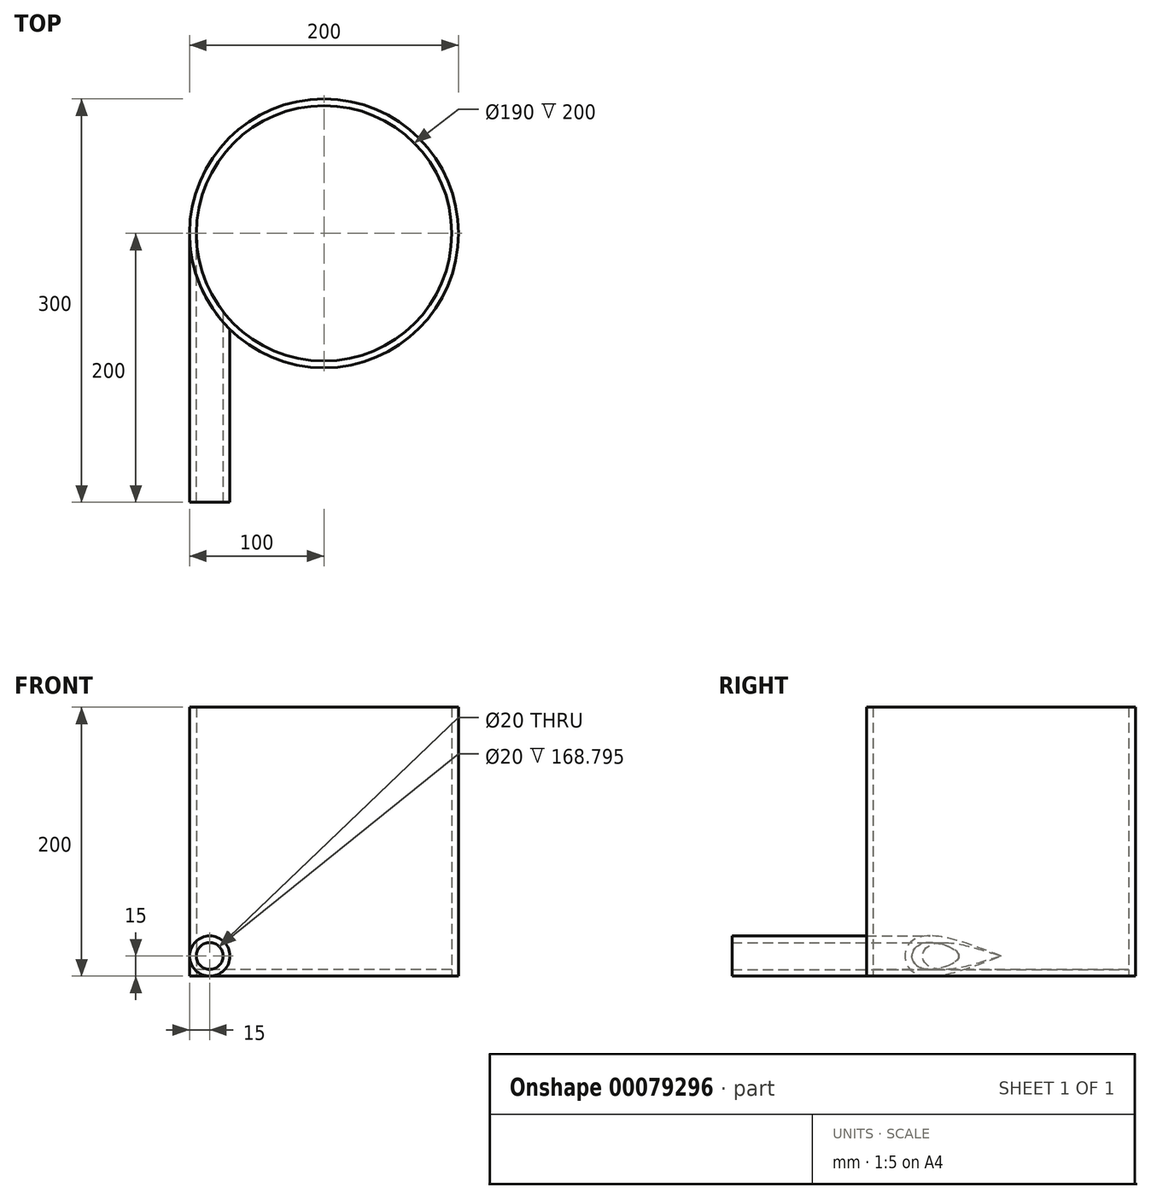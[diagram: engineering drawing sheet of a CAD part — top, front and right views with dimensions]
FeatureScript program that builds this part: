
annotation { "Feature Type Name" : "Feature", "Feature Type Description" : "" }
export const myFeature = defineFeature(function(context is Context, id is Id, definition is map)
    precondition{}
    {
        {
            var Q0;
            Q0=qCreatedBy(makeId("Front.planeOp"),FACE);
            var sketch = newSketch(context, id + "F0", { "sketchPlane" : qUnion([Q0])});
            skCircle(sketch, "E0", {"center": v(-85, 15) * mm, "radius": 10 * mm});
            skPoint(sketch, "E1.orphan", {"position": v(0, 15) * mm});
            skPoint(sketch, "E2.end.orphan", {"position": v(-85, 0) * mm});
            skCircle(sketch, "E3", {"center": v(-85, 15) * mm, "radius": 15 * mm});
            skSolve(sketch);
        }
        {
            var Q0;
            Q0=makeQuery(id+"F0.imprint","IMPRINT",FACE,{"disambiguationData":[TD([[makeQuery(id+"F0.imprint","IMPRINT",EDGE,{"derivedFrom":sQuery(id+"F0.wireOp",EDGE,"E0")}),-1.0]])]});
            extrude(context, id + "F1", {"entities" : qUnion([Q0]), "depth" : 200 * mm});
        }
        {
            var Q0;
            Q0=qCreatedBy(makeId("Top.planeOp"),FACE);
            cPlane(context, id + "F2", {"entities" : qUnion([Q0]), "cplaneType" : CPlaneType.OFFSET, "offset" : 20 * mm, "oppositeDirection" : true, "width" : 150 * mm, "height" : 150 * mm});
        }
        {
            var Q0;
            Q0=qCreatedBy(id+"F2.planeOp",FACE);
            var sketch = newSketch(context, id + "F3", { "sketchPlane" : qUnion([Q0])});
            skCircle(sketch, "E4", {"center": v(0, 0) * mm, "radius": 100 * mm});
            skLineSegment(sketch, "E5.bottom", {"start": v(-300.59, 221.19) * mm, "end": v(271.5, 221.19) * mm});
            skLineSegment(sketch, "E5.top", {"start": v(-300.59, -236.18) * mm, "end": v(271.5, -236.18) * mm});
            skLineSegment(sketch, "E5.left", {"start": v(-300.59, 221.19) * mm, "end": v(-300.59, -236.18) * mm});
            skLineSegment(sketch, "E5.right", {"start": v(271.5, 221.19) * mm, "end": v(271.5, -236.18) * mm});
            skSolve(sketch);
        }
        {
            var Q0;
            Q0=makeQuery(id+"F3.imprint","IMPRINT",FACE,{"disambiguationData":[TD([[makeQuery(id+"F3.imprint","IMPRINT",EDGE,{"derivedFrom":sQuery(id+"F3.wireOp",EDGE,"E4")}),-1.0]])]});
            extrude(context, id + "F4", {"entities" : qUnion([Q0]), "operationType" : NewBodyOperationType.INTERSECT, "depth" : 60 * mm});
        }
        {
            var Q0;
            Q0=qCreatedBy(makeId("Front.planeOp"),FACE);
            var sketch = newSketch(context, id + "F5", { "sketchPlane" : qUnion([Q0])});
            skCircle(sketch, "E6", {"center": v(-85, 15) * mm, "radius": 10 * mm});
            skPoint(sketch, "E7.orphan", {"position": v(0, 15) * mm});
            skPoint(sketch, "E8.end.orphan", {"position": v(-85, 0) * mm});
            skSolve(sketch);
        }
        {
            var Q0;
            Q0=qCreatedBy(makeId("Top.planeOp"),FACE);
            var sketch = newSketch(context, id + "F6", { "sketchPlane" : qUnion([Q0])});
            skCircle(sketch, "E9", {"center": v(0, 0) * mm, "radius": 100 * mm});
            skCircle(sketch, "E10", {"center": v(0, 0) * mm, "radius": 95 * mm});
            skSolve(sketch);
        }
        {
            var Q0;
            Q0=makeQuery(id+"F6.imprint","IMPRINT",FACE,{"disambiguationData":[TD([[makeQuery(id+"F6.imprint","IMPRINT",EDGE,{"derivedFrom":sQuery(id+"F6.wireOp",EDGE,"E10")}),1.0]])]});
            extrude(context, id + "F7", {"entities" : qUnion([Q0]), "depth" : 5 * mm});
        }
        {
            var Q0;
            Q0=makeQuery(id+"F6.imprint","IMPRINT",FACE,{"disambiguationData":[TD([[makeQuery(id+"F6.imprint","IMPRINT",EDGE,{"derivedFrom":sQuery(id+"F6.wireOp",EDGE,"E9")}),1.0]])]});
            extrude(context, id + "F8", {"entities" : qUnion([Q0]), "depth" : 200 * mm});
        }
        {
            var Q0;
            Q0=sQuery(id+"F5.wireOp",VERTEX,"E6.center");
            var Q1;
            Q1=makeQuery(id+"F8.opExtrude","SWEPT_BODY",BODY,{"disambiguationData":[OSD([sQuery(id+"F6.wireOp",EDGE,"E9"),sQuery(id+"F6.wireOp",EDGE,"E10")])]});
            hole(context, id + "F9", {"style" : HoleStyle.SIMPLE, "endStyle" : HoleEndStyle.THROUGH, "oppositeDirection" : true, "holeDiameter" : 20 * mm, "locations" : qUnion([Q0]), "scope" : qUnion([Q1]), "isTappedThrough" : true});
        }
    });
